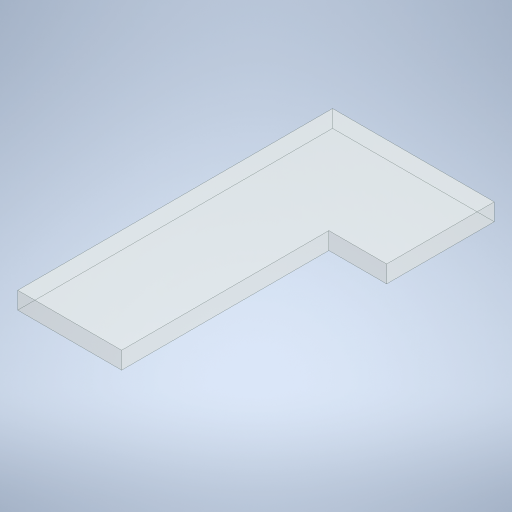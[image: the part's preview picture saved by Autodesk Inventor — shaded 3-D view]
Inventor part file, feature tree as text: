
AUTODESK INVENTOR PART (.ipt)
format: ipt  version: 2024 (Build 280153000, 153)  size: 234,496 bytes
history: native  units: in
note: dims shown in document units (in); Inventor stores cm internally (conversion verified against a paired STEP export)
features: extrude x1, sketch x1
ambient origin geometry x8: Origin, YZ Plane, XZ Plane, XY Plane, X Axis, Y Axis, Z Axis, Center Point
bodies: Solid1 (feature_tree)
feature tree (2):
  extrude  "Extrusion1"  Depth=32.875in
  sketch  "Sketch1"  dims[d1=21.125in d2=32.875in d3=21.875in d6=3.5in d7=0.0in d9=42.125in d10=64.0in d11=11.75in]
